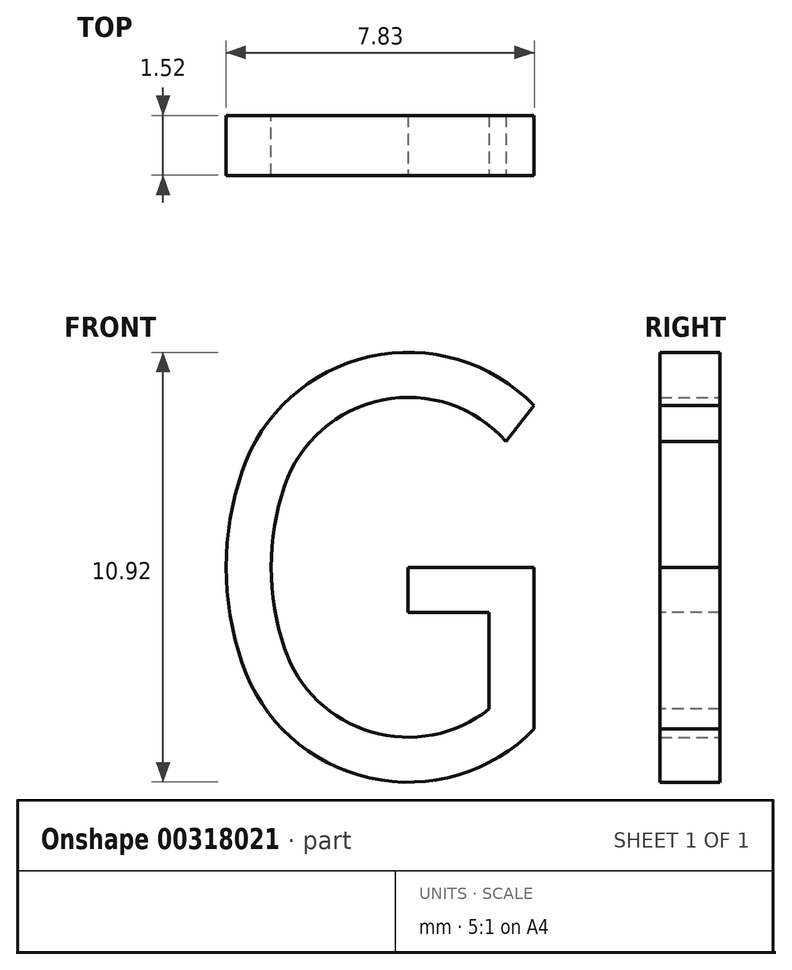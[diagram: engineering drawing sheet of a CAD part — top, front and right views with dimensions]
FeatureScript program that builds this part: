
annotation { "Feature Type Name" : "Feature", "Feature Type Description" : "" }
export const myFeature = defineFeature(function(context is Context, id is Id, definition is map)
    precondition{}
    {
        {
            var Q0;
            Q0=qCreatedBy(makeId("Front.planeOp"),FACE);
            var sketch = newSketch(context, id + "F0", { "sketchPlane" : qUnion([Q0])});
            skArc(sketch, "E0.0.0", {"start": v(-8.23, 24.3) * mm, "mid": v(-7.83, 26.74) * mm, "end": v(-8.23, 29.17) * mm});
            skArc(sketch, "E0.0.1", {"start": v(-8.23, 29.17) * mm, "mid": v(-12.45, 32.2) * mm, "end": v(-16.68, 29.17) * mm});
            skArc(sketch, "E0.0.2", {"start": v(-16.68, 29.17) * mm, "mid": v(-17.08, 26.74) * mm, "end": v(-16.68, 24.3) * mm});
            skArc(sketch, "E0.0.3", {"start": v(-16.68, 24.3) * mm, "mid": v(-12.45, 21.28) * mm, "end": v(-8.23, 24.3) * mm});
            skArc(sketch, "E1.0", {"start": v(-9.31, 28.8) * mm, "mid": v(-12.45, 31.06) * mm, "end": v(-15.6, 28.8) * mm});
            skArc(sketch, "E1.1", {"start": v(-15.6, 28.8) * mm, "mid": v(-15.93, 26.74) * mm, "end": v(-15.6, 24.67) * mm});
            skArc(sketch, "E1.2", {"start": v(-15.6, 24.67) * mm, "mid": v(-12.45, 22.42) * mm, "end": v(-9.31, 24.67) * mm});
            skArc(sketch, "E1.3", {"start": v(-9.31, 24.67) * mm, "mid": v(-8.97, 26.74) * mm, "end": v(-9.31, 28.8) * mm});
            skPoint(sketch, "E2", {"position": v(-7.83, 26.74) * mm});
            skPoint(sketch, "E3", {"position": v(-8.97, 26.74) * mm});
            skPoint(sketch, "E4", {"position": v(-15.93, 26.74) * mm});
            skPoint(sketch, "E5", {"position": v(-17.08, 26.74) * mm});
            skPoint(sketch, "E6", {"position": v(-12.45, 31.06) * mm});
            skPoint(sketch, "E7", {"position": v(-12.45, 32.2) * mm});
            skPoint(sketch, "E8", {"position": v(-12.45, 22.42) * mm});
            skPoint(sketch, "E9", {"position": v(-12.45, 21.28) * mm});
            skPoint(sketch, "E10", {"position": v(2.18, 11.12) * mm});
            skSolve(sketch);
        }
        {
            var Q0;
            Q0 = qSketchRegion(id + "F0", true);
            extrude(context, id + "F1", {"entities" : qUnion([Q0]), "depth" : 1.52 * mm});
        }
        {
            var Q0;
            Q0=makeQuery(id+"F1.opExtrude","CAP_FACE",FACE,{"disambiguationData":[OSD([sQuery(id+"F0.wireOp",EDGE,"E0.0.0"),sQuery(id+"F0.wireOp",EDGE,"E0.0.1"),sQuery(id+"F0.wireOp",EDGE,"E0.0.2"),sQuery(id+"F0.wireOp",EDGE,"E0.0.3"),sQuery(id+"F0.wireOp",EDGE,"E1.0"),sQuery(id+"F0.wireOp",EDGE,"E1.1"),sQuery(id+"F0.wireOp",EDGE,"E1.2"),sQuery(id+"F0.wireOp",EDGE,"E1.3")])],"isStart":false});
            var sketch = newSketch(context, id + "F2", { "sketchPlane" : qUnion([Q0])});
            skLineSegment(sketch, "E11", {"start": v(-9.25, 22.63) * mm, "end": v(-9.25, 24.86) * mm});
            skPoint(sketch, "E11.endSnap0", {"position": v(-8.97, 26.74) * mm});
            skLineSegment(sketch, "E12", {"start": v(-9.25, 26.74) * mm, "end": v(-12.45, 26.74) * mm});
            skPoint(sketch, "E12.endSnap0", {"position": v(-12.45, 32.2) * mm});
            skPoint(sketch, "E13.0", {"position": v(-15.93, 26.74) * mm});
            skPoint(sketch, "E14.0", {"position": v(-17.08, 26.74) * mm});
            skLineSegment(sketch, "E15.0", {"start": v(-10.4, 25.6) * mm, "end": v(-12.45, 25.6) * mm});
            skLineSegment(sketch, "E15.1", {"start": v(-10.4, 23.14) * mm, "end": v(-10.4, 25.6) * mm});
            skLineSegment(sketch, "E16", {"start": v(-12.45, 25.6) * mm, "end": v(-12.45, 26.74) * mm});
            skArc(sketch, "E17.0", {"start": v(-9.31, 24.67) * mm, "mid": v(-8.97, 26.74) * mm, "end": v(-9.31, 28.8) * mm});
            skArc(sketch, "E18.0", {"start": v(-15.6, 24.67) * mm, "mid": v(-12.45, 22.42) * mm, "end": v(-9.31, 24.67) * mm});
            skLineSegment(sketch, "E19", {"start": v(-9.25, 26.74) * mm, "end": v(-9.25, 24.86) * mm});
            skLineSegment(sketch, "E20", {"start": v(-9.97, 29.93) * mm, "end": v(-9.26, 30.85) * mm});
            skArc(sketch, "E21.0", {"start": v(-9.31, 28.8) * mm, "mid": v(-12.45, 31.06) * mm, "end": v(-15.6, 28.8) * mm});
            skSolve(sketch);
        }
        {
            var Q0;
            Q0=makeQuery(id+"F2.imprint","IMPRINT",FACE,{"disambiguationData":[TD([[makeQuery(id+"F2.imprint","IMPRINT",EDGE,{"derivedFrom":sQuery(id+"F2.wireOp",EDGE,"E12")}),1.0]])]});
            extrude(context, id + "F3", {"entities" : qUnion([Q0]), "operationType" : NewBodyOperationType.ADD, "oppositeDirection" : true, "depth" : 1.52 * mm});
        }
        {
            var Q0;
            {var subQ4=sQuery(id+"F2.wireOp",EDGE,"E11");Q0=makeQuery(id+"F2.imprint","IMPRINT",FACE,{"disambiguationData":[TD([[makeQuery(id+"F2.imprint","IMPRINT",EDGE,{"derivedFrom":subQ4}),-1.0]])]});}
            extrude(context, id + "F4", {"entities" : qUnion([Q0]), "operationType" : NewBodyOperationType.REMOVE, "oppositeDirection" : true, "depth" : 25.4 * mm});
        }
    });
